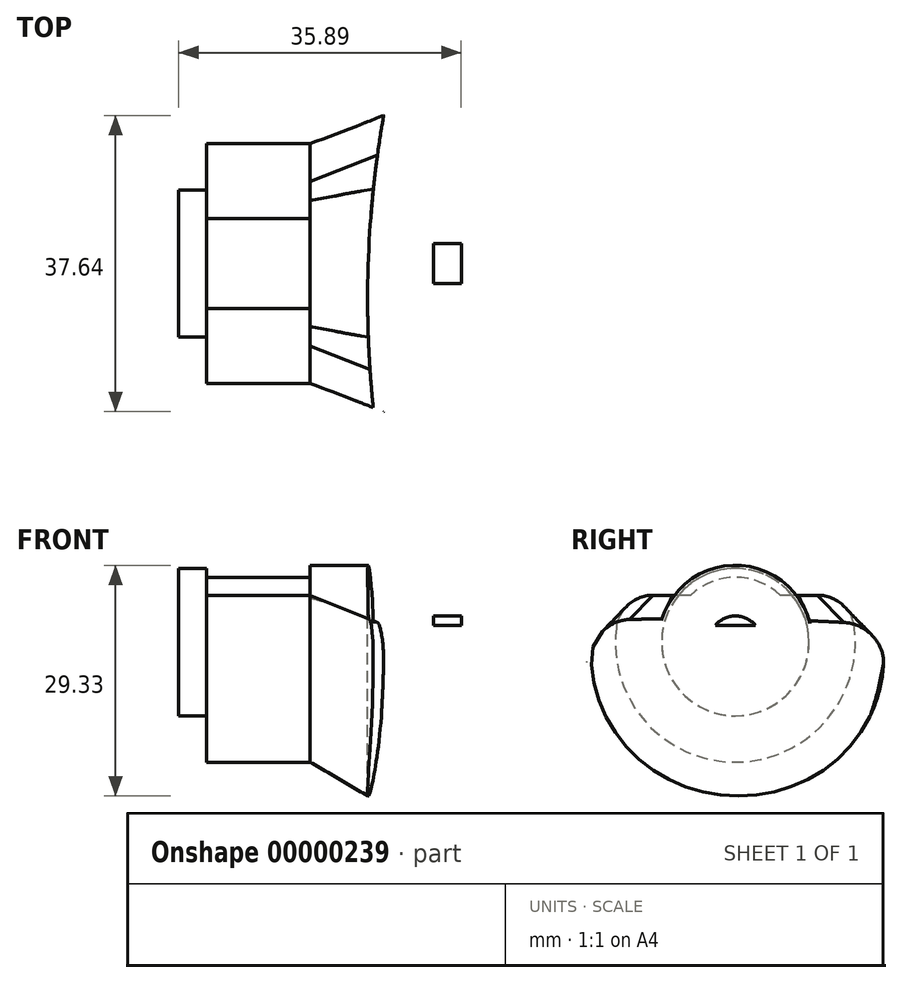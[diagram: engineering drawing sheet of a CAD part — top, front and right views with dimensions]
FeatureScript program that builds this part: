
annotation { "Feature Type Name" : "Feature", "Feature Type Description" : "" }
export const myFeature = defineFeature(function(context is Context, id is Id, definition is map)
    precondition{}
    {
        {
            var Q0;
            Q0=qCreatedBy(makeId("Right.planeOp"),FACE);
            var sketch = newSketch(context, id + "F0", { "sketchPlane" : qUnion([Q0])});
            skLineSegment(sketch, "E0", {"start": v(-14.13, 0) * mm, "end": v(14.13, 0) * mm});
            skArc(sketch, "E1", {"start": v(-18.84, -4.95) * mm, "mid": v(0, -22.89) * mm, "end": v(18.84, -4.95) * mm});
            skPoint(sketch, "E2.visualSharp", {"position": v(-18.43, 0) * mm});
            skArc(sketch, "E2.filletArc", {"start": v(-14.13, 0) * mm, "mid": v(-17.55, -1.46) * mm, "end": v(-18.84, -4.95) * mm});
            skPoint(sketch, "E3.visualSharp", {"position": v(18.43, 0) * mm});
            skArc(sketch, "E3.filletArc", {"start": v(18.84, -4.95) * mm, "mid": v(17.55, -1.46) * mm, "end": v(14.13, 0) * mm});
            skLineSegment(sketch, "E4", {"start": v(-9.73, 0) * mm, "end": v(-9.73, -8.64) * mm});
            skLineSegment(sketch, "E5", {"start": v(9.73, 0) * mm, "end": v(9.73, -8.64) * mm});
            skArc(sketch, "E6", {"start": v(-9.73, -8.64) * mm, "mid": v(0, -11.94) * mm, "end": v(9.73, -8.64) * mm});
            skCircle(sketch, "E7", {"center": v(0, -2.16) * mm, "radius": 9.78 * mm, "construction": true});
            skSolve(sketch);
        }
        {
            var Q0;
            Q0=makeQuery(id+"F0.imprint","IMPRINT",FACE,{"disambiguationData":[TD([[makeQuery(id+"F0.imprint","IMPRINT",EDGE,{"derivedFrom":sQuery(id+"F0.wireOp",EDGE,"E1")}),1.0]])]});
            extrude(context, id + "F1", {"entities" : qUnion([Q0]), "depth" : 4 * mm});
        }
        {
            var Q0;
            Q0=sQuery(id+"F0.wireOp",VERTEX,"E7.center");
            var Q1;
            {var subQ0=sQuery(id+"F0.wireOp",EDGE,"E0");Q1=makeQuery(id+"F1.opExtrude","SWEPT_FACE",FACE,{"disambiguationData":[OSD([subQ0]),TDD([makeQuery(id+"F0.imprint","IMPRINT",EDGE,{"disambiguationData":[TD([[makeQuery(id+"F0.imprint","INTERSECT",VERTEX,{"derivedFrom":[subQ0,sQuery(id+"F0.wireOp",EDGE,"E2.filletArc")]}),-1.0]])],"derivedFrom":subQ0})])]});}
            cPlane(context, id + "F2", {"entities" : qUnion([Q0, Q1]), "cplaneType" : CPlaneType.PLANE_POINT, "offset" : 25.4 * mm, "width" : 152.4 * mm, "height" : 152.4 * mm});
        }
        {
            var Q0;
            Q0=qCreatedBy(id+"F2.planeOp",FACE);
            var sketch = newSketch(context, id + "F3", { "sketchPlane" : qUnion([Q0])});
            skLineSegment(sketch, "E8", {"start": v(-26.09, 0) * mm, "end": v(9.8, 0) * mm});
            skLineSegment(sketch, "E9", {"start": v(9.8, 0) * mm, "end": v(9.8, -3.33) * mm});
            skLineSegment(sketch, "E10", {"start": v(9.8, -3.33) * mm, "end": v(3.99, -3.33) * mm});
            skLineSegment(sketch, "E11", {"start": v(3.99, -3.33) * mm, "end": v(3.99, -9.78) * mm});
            skLineSegment(sketch, "E12", {"start": v(3.99, -9.78) * mm, "end": v(-9.4, -9.78) * mm});
            skLineSegment(sketch, "E13", {"start": v(-9.4, -9.78) * mm, "end": v(-9.4, -8.26) * mm});
            skLineSegment(sketch, "E14", {"start": v(-9.4, -8.26) * mm, "end": v(-22.58, -8.26) * mm});
            skLineSegment(sketch, "E15", {"start": v(-22.58, -8.26) * mm, "end": v(-22.58, -9.36) * mm});
            skLineSegment(sketch, "E16", {"start": v(-22.58, -9.36) * mm, "end": v(-26.09, -9.36) * mm});
            skLineSegment(sketch, "E17", {"start": v(-26.09, -9.36) * mm, "end": v(-26.09, 0) * mm});
            skSolve(sketch);
        }
        {
            var Q0;
            Q0 = qSketchRegion(id + "F3", true);
            var Q1;
            Q1=sQuery(id+"F3.wireOp",EDGE,"E8");
            revolve(context, id + "F4", {"entities" : qUnion([Q0]), "axis" : qUnion([Q1]), "revolveType" : RevolveType.FULL});
        }
        {
            var Q0;
            Q0=makeQuery(id+"F4.opRevolve","SWEPT_FACE",FACE,{"disambiguationData":[OSD([sQuery(id+"F3.wireOp",EDGE,"E13")])]});
            var sketch = newSketch(context, id + "F5", { "sketchPlane" : qUnion([Q0])});
            skArc(sketch, "E18.0", {"start": v(7.75, 3.8) * mm, "mid": v(0, -11.94) * mm, "end": v(-7.75, 3.8) * mm});
            skLineSegment(sketch, "E19", {"start": v(-10.45, 3.81) * mm, "end": v(-7.75, 3.81) * mm});
            skArc(sketch, "E20", {"start": v(-15.13, -0.35) * mm, "mid": v(0, -17.4) * mm, "end": v(15.13, -0.35) * mm});
            skLineSegment(sketch, "E21.trimOffspring", {"start": v(7.75, 3.81) * mm, "end": v(10.45, 3.81) * mm});
            skPoint(sketch, "E22.visualSharp", {"position": v(-14.02, 3.81) * mm});
            skArc(sketch, "E22.filletArc", {"start": v(-10.45, 3.81) * mm, "mid": v(-13.58, 2.62) * mm, "end": v(-15.13, -0.35) * mm});
            skPoint(sketch, "E23.visualSharp", {"position": v(14.02, 3.81) * mm});
            skArc(sketch, "E23.filletArc", {"start": v(15.13, -0.35) * mm, "mid": v(13.58, 2.62) * mm, "end": v(10.45, 3.8) * mm});
            skLineSegment(sketch, "E24", {"start": v(-8, 3.81) * mm, "end": v(-8, 3.47) * mm});
            skLineSegment(sketch, "E25", {"start": v(8, 3.81) * mm, "end": v(8, 3.47) * mm});
            skSolve(sketch);
        }
        {
            var Q0;
            Q0=makeQuery(id+"F0.imprint","IMPRINT",FACE,{"disambiguationData":[TD([[makeQuery(id+"F0.imprint","IMPRINT",EDGE,{"derivedFrom":sQuery(id+"F0.wireOp",EDGE,"E1")}),1.0]])]});
            var sketch = newSketch(context, id + "F6", { "sketchPlane" : qUnion([Q0])});
            skArc(sketch, "E26.0", {"start": v(-7.75, 3.8) * mm, "mid": v(0, -11.94) * mm, "end": v(7.75, 3.8) * mm});
            skLineSegment(sketch, "E27.0", {"start": v(9.73, 0) * mm, "end": v(9.73, -8.64) * mm});
            skArc(sketch, "E27.1", {"start": v(-9.73, -8.64) * mm, "mid": v(0, -11.94) * mm, "end": v(9.73, -8.64) * mm});
            skLineSegment(sketch, "E27.2", {"start": v(-9.73, 0) * mm, "end": v(-9.73, -8.64) * mm});
            skSolve(sketch);
        }
        {
            var Q0;
            {var subQ0=sQuery(id+"F6.wireOp",EDGE,"E27.1");var subQ1=sQuery(id+"F6.wireOp",EDGE,"E26.0");var subQ2=makeQuery(id+"F6.imprint","INTERSECT",VERTEX,{"derivedFrom":[subQ1,subQ0]});Q0=makeQuery(id+"F6.imprint","IMPRINT",FACE,{"disambiguationData":[TD([[makeQuery(id+"F6.imprint","IMPRINT",EDGE,{"disambiguationData":[TD([[subQ2,-1.0]])],"derivedFrom":subQ1}),-1.0]])]});}
            var Q1;
            {var subQ0=sQuery(id+"F6.wireOp",EDGE,"E27.2");var subQ1=sQuery(id+"F6.wireOp",EDGE,"E26.0");var subQ2=makeQuery(id+"F6.imprint","INTERSECT",VERTEX,{"disambiguationData":[OD(1.0)],"derivedFrom":[subQ1,subQ0]});Q1=makeQuery(id+"F6.imprint","IMPRINT",FACE,{"disambiguationData":[TD([[makeQuery(id+"F6.imprint","IMPRINT",EDGE,{"disambiguationData":[TD([[subQ2,-1.0]])],"derivedFrom":subQ1}),-1.0]])]});}
            var Q2;
            Q2=makeQuery(id+"F1.opExtrude","CAP_FACE",FACE,{"disambiguationData":[OSD([sQuery(id+"F0.wireOp",EDGE,"E0"),sQuery(id+"F0.wireOp",EDGE,"E1"),sQuery(id+"F0.wireOp",EDGE,"E2.filletArc"),sQuery(id+"F0.wireOp",EDGE,"E3.filletArc"),sQuery(id+"F0.wireOp",EDGE,"E4"),sQuery(id+"F0.wireOp",EDGE,"E5"),sQuery(id+"F0.wireOp",EDGE,"E6")])],"isStart":false});
            extrude(context, id + "F7", {"entities" : qUnion([Q0, Q1]), "operationType" : NewBodyOperationType.ADD, "endBound" : BoundingType.UP_TO_SURFACE, "endBoundEntityFace" : qUnion([Q2]), "depth" : 25.4 * mm});
        }
        {
            var Q0;
            Q0=makeQuery(id+"F1.opExtrude","CAP_VERTEX",VERTEX,{"disambiguationData":[OSD([sQuery(id+"F0.wireOp",EDGE,"E0"),sQuery(id+"F0.wireOp",EDGE,"E5")])],"isStart":true});
            var Q1;
            Q1=sQuery(id+"F5.wireOp",VERTEX,"E19.end");
            var Q2;
            Q2=makeQuery(id+"F1.opExtrude","CAP_VERTEX",VERTEX,{"disambiguationData":[OSD([sQuery(id+"F0.wireOp",EDGE,"E0"),sQuery(id+"F0.wireOp",EDGE,"E3.filletArc")])],"isStart":true});
            cPlane(context, id + "F8", {"entities" : qUnion([Q0, Q1, Q2]), "cplaneType" : CPlaneType.THREE_POINT, "offset" : 25.4 * mm, "width" : 152.4 * mm, "height" : 152.4 * mm});
        }
        {
            var Q0;
            Q0=qCreatedBy(id+"F8.planeOp",FACE);
            var sketch = newSketch(context, id + "F9", { "sketchPlane" : qUnion([Q0])});
            skLineSegment(sketch, "E28", {"start": v(0, 9.73) * mm, "end": v(-10.14, 7.75) * mm});
            skSolve(sketch);
        }
        {
            var Q0;
            {var subQ0=sQuery(id+"F6.wireOp",EDGE,"E27.1");var subQ1=sQuery(id+"F6.wireOp",EDGE,"E26.0");Q0=makeQuery(id+"F7.boolean.opBoolean","MERGE",FACE,{"derivedFrom":[makeQuery(id+"F1.opExtrude","CAP_FACE",FACE,{"disambiguationData":[OSD([sQuery(id+"F0.wireOp",EDGE,"E0"),sQuery(id+"F0.wireOp",EDGE,"E1"),sQuery(id+"F0.wireOp",EDGE,"E2.filletArc"),sQuery(id+"F0.wireOp",EDGE,"E3.filletArc"),sQuery(id+"F0.wireOp",EDGE,"E4"),sQuery(id+"F0.wireOp",EDGE,"E5"),sQuery(id+"F0.wireOp",EDGE,"E6")])],"isStart":true}),makeQuery(id+"F7.opExtrude","CAP_FACE",FACE,{"disambiguationData":[OSD([subQ1,subQ0,sQuery(id+"F6.wireOp",EDGE,"E27.2")])],"isStart":true}),makeQuery(id+"F7.opExtrude","CAP_FACE",FACE,{"disambiguationData":[OSD([subQ1,sQuery(id+"F6.wireOp",EDGE,"E27.0"),subQ0])],"isStart":true})]});}
            var Q1;
            Q1=makeQuery(id+"F5.imprint","IMPRINT",FACE,{"disambiguationData":[TD([[makeQuery(id+"F5.imprint","IMPRINT",EDGE,{"derivedFrom":sQuery(id+"F5.wireOp",EDGE,"E20")}),1.0]])]});
            loft(context, id + "F10", {"sheetProfilesArray" : [{ "sheetProfileEntities" : qUnion([Q0]) }, { "sheetProfileEntities" : qUnion([Q1]) }]});
        }
        {
            var Q0;
            Q0=makeQuery(id+"F5.imprint","IMPRINT",FACE,{"disambiguationData":[TD([[makeQuery(id+"F5.imprint","IMPRINT",EDGE,{"derivedFrom":sQuery(id+"F5.wireOp",EDGE,"E20")}),1.0]])]});
            var sketch = newSketch(context, id + "F11", { "sketchPlane" : qUnion([Q0])});
            skArc(sketch, "E29.0", {"start": v(-5.7, 3.8) * mm, "mid": v(0, -10.41) * mm, "end": v(5.7, 3.81) * mm});
            skLineSegment(sketch, "E30", {"start": v(-10.45, 3.81) * mm, "end": v(-5.7, 3.81) * mm});
            skArc(sketch, "E31.0", {"start": v(-10.45, 3.81) * mm, "mid": v(-13.58, 2.62) * mm, "end": v(-15.13, -0.35) * mm});
            skArc(sketch, "E31.1", {"start": v(-15.13, -0.35) * mm, "mid": v(0, -17.4) * mm, "end": v(15.13, -0.35) * mm});
            skArc(sketch, "E31.2", {"start": v(15.13, -0.35) * mm, "mid": v(13.58, 2.62) * mm, "end": v(10.45, 3.81) * mm});
            skLineSegment(sketch, "E32.trimOffspring", {"start": v(5.7, 3.81) * mm, "end": v(10.45, 3.81) * mm});
            skSolve(sketch);
        }
        {
            var Q0;
            Q0 = qSketchRegion(id + "F11", true);
            var Q1;
            Q1=makeQuery(id+"F4.opRevolve","SWEPT_FACE",FACE,{"disambiguationData":[OSD([sQuery(id+"F3.wireOp",EDGE,"E15")])]});
            extrude(context, id + "F12", {"entities" : qUnion([Q0]), "operationType" : NewBodyOperationType.ADD, "endBound" : BoundingType.UP_TO_SURFACE, "endBoundEntityFace" : qUnion([Q1]), "depth" : 25.4 * mm});
        }
        {
            var Q0;
            Q0=qCreatedBy(makeId("Front.planeOp"),FACE);
            var sketch = newSketch(context, id + "F13", { "sketchPlane" : qUnion([Q0])});
            skArc(sketch, "E33", {"start": v(-21.32, -88.35) * mm, "mid": v(-0.75, -16.98) * mm, "end": v(-8.54, 56.89) * mm});
            skPoint(sketch, "E34", {"position": v(-1.27, -22.14) * mm});
            skLineSegment(sketch, "E35", {"start": v(-9.4, -17.4) * mm, "end": v(0, -22.89) * mm, "construction": true});
            skLineSegment(sketch, "E36", {"start": v(0, 0) * mm, "end": v(15.76, 0) * mm});
            skLineSegment(sketch, "E37", {"start": v(15.76, 0) * mm, "end": v(15.76, -22.89) * mm});
            skLineSegment(sketch, "E38", {"start": v(15.76, -22.89) * mm, "end": v(-1.36, -22.89) * mm});
            skSolve(sketch);
        }
        {
            var Q0;
            Q0 = qSketchRegion(id + "F13", true);
            extrude(context, id + "F14", {"entities" : qUnion([Q0]), "operationType" : NewBodyOperationType.REMOVE, "oppositeDirection" : true, "depth" : 50.8 * mm, "symmetric" : true});
        }
        {
            var Q0;
            Q0=qCreatedBy(makeId("Top.planeOp"),FACE);
            var sketch = newSketch(context, id + "F15", { "sketchPlane" : qUnion([Q0])});
            skArc(sketch, "E39", {"start": v(-1.32, -18.82) * mm, "mid": v(0, 0) * mm, "end": v(-1.32, 18.82) * mm, "construction": true});
            skLineSegment(sketch, "E40", {"start": v(-0.05, 18.82) * mm, "end": v(-11.66, 18.82) * mm});
            skLineSegment(sketch, "E41", {"start": v(0, 0) * mm, "end": v(-5.7, 0) * mm, "construction": true});
            skLineSegment(sketch, "E42", {"start": v(-1.32, -18.82) * mm, "end": v(6.3, -18.82) * mm});
            skLineSegment(sketch, "E43", {"start": v(6.3, -18.82) * mm, "end": v(6.3, 18.82) * mm});
            skLineSegment(sketch, "E44", {"start": v(6.3, 18.82) * mm, "end": v(-0.05, 18.82) * mm});
            skArc(sketch, "E45", {"start": v(-0.05, 18.82) * mm, "mid": v(-2.01, 0.04) * mm, "end": v(-1.32, -18.82) * mm});
            skSolve(sketch);
        }
        {
            var Q0;
            Q0 = qSketchRegion(id + "F15", true);
            extrude(context, id + "F16", {"entities" : qUnion([Q0]), "operationType" : NewBodyOperationType.REMOVE, "oppositeDirection" : true, "depth" : 50.8 * mm, "symmetric" : true});
        }
    });
